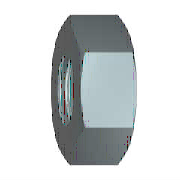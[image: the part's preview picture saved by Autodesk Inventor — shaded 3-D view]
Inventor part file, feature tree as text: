
AUTODESK INVENTOR PART (.ipt)
format: ipt  version: 2015 (Build 190159000, 159)  size: 161,792 bytes
history: native  units: mm (DEFAULTED — no unit token found)
features: sketch x3, chamfer x1, hole x1, other x1, plane x1
ambient origin geometry x7: Origin, YZ Plane, XZ Plane, X Axis, Y Axis, Z Axis, Center Point
bodies: Solid1 (feature_tree), Body (feature_tree)
feature tree (7):
  chamfer  "Chamfer1"  Angle=30.0deg  [1 undecoded]
  hole  "Thread"  [1 undecoded]
  other  "Work Axis1"
  plane  "Work Plane1"
  sketch  "Sketch1"  dims[d0=9.237604mm]
  sketch  "Sketch2"  dims[d1=5.1mm]
  sketch  "Sketch3"  dims[d2=0.0mm d3=30.0deg d4=30.0deg d5=6.9mm d6=6.9mm d7=90.0deg d25=4.134mm d26=6.0mm d27=4.0mm d28=2.0mm d29=14.3117mm d30=8.0mm d31=20.594885mm d8=0.433013mm d9=30.0deg d10=0.433013mm d11=30.0deg d13=0.0mm d14=0.0mm d39=0.0mm d40=0.433013mm d41=0.433013mm d42=0.0mm]
note: 2 required parameter values undecoded (feature->parameter linkage not recoverable at this tier; creation-order binding heuristic only, values carry confidence <= 0.55)
